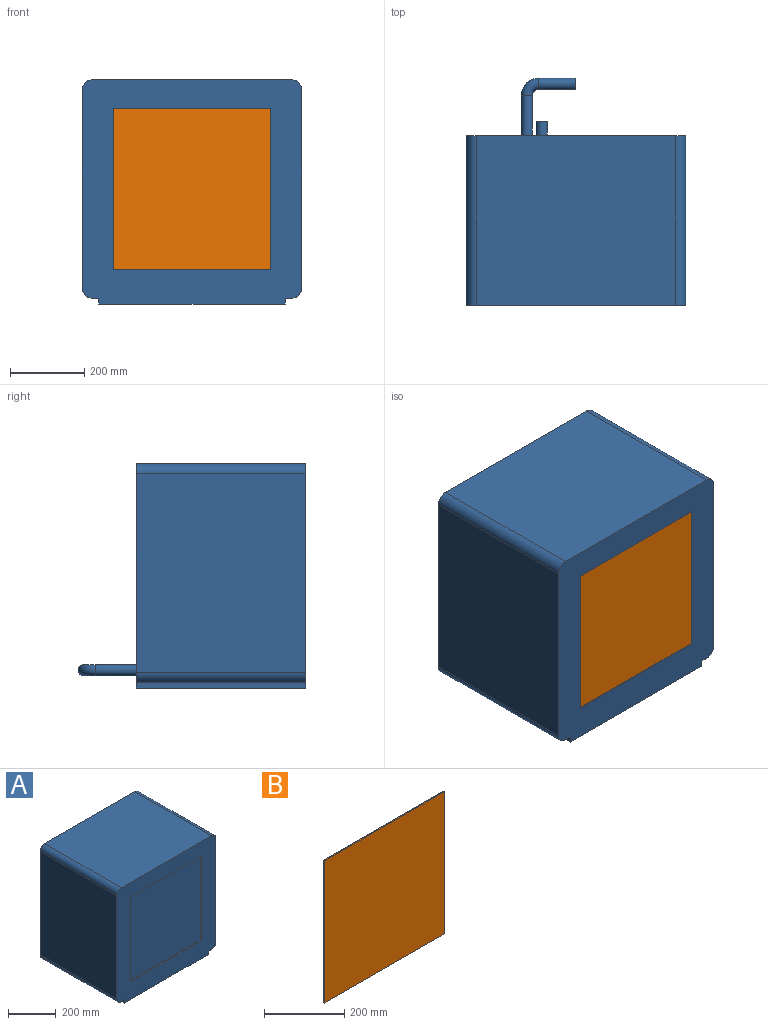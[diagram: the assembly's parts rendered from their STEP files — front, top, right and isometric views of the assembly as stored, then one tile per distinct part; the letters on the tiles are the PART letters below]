
ASSEMBLY  parts=2 mates=1
PART A: 25 faces, bbox 590x614.5x603 mm
  f0: plane 603x590mm, normal (0,-1,0), area 169607.7mm2, adj f1,f2,f3,f4,f5,f6,f7,f8
  f1: plane 455.5x18mm, normal (0,0,-1), area 8199mm2, adj f0,f2,f12,f13
  f2: plane 455.5x16mm, normal (-1,0,0), area 7288mm2, adj f0,f1,f3,f13
  f3: plane 500x455.5mm, normal (0,0,-1), area 227750mm2, adj f0,f2,f4,f13
  f4: plane 455.5x16mm, normal (1,0,0), area 7288mm2, adj f0,f3,f5,f13
  f5: plane 455.5x18mm, normal (0,0,-1), area 8199mm2, adj f0,f4,f6,f13
  f6: cylinder r=27mm len=455.5mm, axis (0,-1,0), area 19318.4mm2, adj f0,f5,f7,f13
  f7: plane 533x455.5mm, normal (1,0,0), area 242781.5mm2, adj f0,f6,f8,f13
  f8: cylinder r=27mm len=455.5mm, axis (0,-1,0), area 19318.4mm2, adj f0,f7,f9,f13
  f9: plane 536x455.5mm, normal (0,0,1), area 244148mm2, adj f0,f8,f10,f13
  f10: cylinder r=27mm len=455.5mm, axis (0,-1,0), area 19318.4mm2, adj f0,f9,f11,f13
  f11: plane 533x455.5mm, normal (-1,0,0), area 242781.5mm2, adj f0,f10,f12,f13
  f12: cylinder r=27mm len=455.5mm, axis (0,-1,0), area 19318.4mm2, adj f0,f1,f11,f13
  f13: plane 603x590mm, normal (0,1,0), area 352290.5mm2, adj f1,f2,f3,f4,f5,f6,f7,f8
  f14: plane 423.6x5mm, normal (0,0,1), area 2118mm2, adj f0,f15,f17,f18
  f15: plane 434.6x5mm, normal (-1,0,0), area 2173mm2, adj f0,f14,f16,f18
  f16: plane 423.6x5mm, normal (0,0,-1), area 2118mm2, adj f0,f15,f17,f18
  f17: plane 434.6x5mm, normal (1,0,0), area 2173mm2, adj f0,f14,f16,f18
  f18: plane 434.6x423.6mm, normal (0,-1,0), area 184096.6mm2, adj f14,f15,f16,f17
  f19: cylinder r=15mm len=40mm, axis (0,-1,0), area 3769.9mm2, adj f13,f20
  f20: plane 30x30mm, normal (0,1,0), area 706.9mm2, adj f19
  f21: cylinder r=15mm len=110mm, axis (0,-1,0), area 10367.3mm2, adj f13,f23
  f22: plane 30x30mm, normal (1,0,0), area 706.9mm2, adj f24
  f23: torus R=30.3mm, axis (0,0,-1), area 4485.7mm2, adj f21,f24
  f24: cylinder r=15mm len=102mm, axis (1,0,0), area 9613.3mm2, adj f22,f23
PART B: 6 faces, bbox 423.6x3x434.6 mm
  f0: plane 423.6x3mm, normal (0,0,-1), area 1270.8mm2, adj f1,f3,f4,f5
  f1: plane 434.6x3mm, normal (1,0,0), area 1303.8mm2, adj f0,f2,f4,f5
  f2: plane 423.6x3mm, normal (0,0,1), area 1270.8mm2, adj f1,f3,f4,f5
  f3: plane 434.6x3mm, normal (-1,0,0), area 1303.8mm2, adj f0,f2,f4,f5
  f4: plane 434.6x423.6mm, normal (0,-1,0), area 184096.6mm2, adj f0,f1,f2,f3
  f5: plane 434.6x423.6mm, normal (0,1,0), area 184096.6mm2, adj f0,f1,f2,f3
PLACE A t=(0,-227.75,309.5)mm
PLACE B t=(0,-222.75,309.5)mm
MATE fastened B.f5 <-> A.f18  axis (0,1,0) through (0,-222.75,309.5)mm
